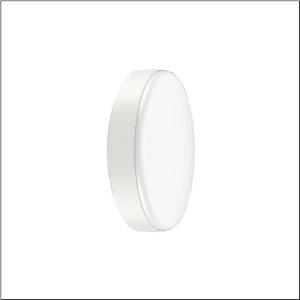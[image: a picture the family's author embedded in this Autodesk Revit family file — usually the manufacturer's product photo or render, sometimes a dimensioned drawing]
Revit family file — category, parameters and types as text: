
# Revit family: rondel_31_51wc10db34as
name_source: partatom
category: Lighting Fixtures
units: mm (PartAtom-declared; Revit-internal decimal feet)

## family parameters
Cut with Voids When Loaded = No
Host = Face
Light Source = No
Part Type = Normal
Room Calculation Point = No
Round Connector Dimension = Use Diameter
Shared = No

## types (1)
- Rondel 31 (1 x LED, 4250 lm, 35.4 W, 3000K)
    Apparent Load = 35 VA
    CIE Flux Codes = 44 75 94 94 100
    Color Rendering = 80
    Color Temperature = 3000K
    Default Elevation = 1800 mm
    Description = Rondel 31, wall and ceiling luminaire, primary optical cover: cover, of PC, opal, light emission: direct distribution, primary light characteristic: symmetric, installation type: surface-mounted, LED, rated luminous flux: 4.250lm, luminous efficacy: 120lm/W, light colour: 830, colour temperature: 3000K, with terminal, 5-pole, max. 2.5mm², mains connection: 220..240V, AC, 50/60Hz, rated input power: 35.5W, luminaire housing, of PC, traffic white (RAL 9016), diameter: 480mm, brightness and presence sensor, HF sensor, protection rating (complete): IP65, insulation class (complete): insulation class II (safety insulation), certification: CE, impact resistance: IK10, permissible operating ambient temperature: -20..+40°C, permissible storage temperature: -20..+60°C, packaging unit: 1 piece
    Height = 97 mm
    Lamp = 1 x LED
    Lamp Light Flux = 4250 lm
    Lamp Power = 35.4 W
    Lamp count = 1
    Length = 480 mm
    Luminous efficacy = 120 lm/W
    Manufacturer = Siteco
    ModVariant = No
    Model = 51WC10DB34AS
    Mounting Place = Ceiling
    Mounting Type = Surface mounted
    Number of Poles = 1
    OnlyDefault = Yes
    Power Factor = 1
    Product Name = Rondel 31
    Product group = wall and ceiling luminaire
    ProductGroupID = 302
    Protection Class = Protection class II
    Protection Degree = IP 65
    RLX_Detail_Level = 1
    RLX_Emergency_Light_Flux = 0 lm
    RLX_Emergency_Type = 0
    RLX_Emergency_Type_DB = No
    RlxData = <blob elided: 40853 chars, md5=f7e8a1e5>
    Socket = socket
    Standby Power = 0 W
    System Light Flux = 4250 lm
    System Power = 35 W
    Type Comments = Product without accessories
    Type Image = l_1007188.jpg
    URL = http://relux.com
    VarID = ---
    Voltage = 0 V
    Weight = 0.00 kg
    Width = 0 mm  [stored 0 ft]

note: [stored X ft] marks values corroborated as IEEE doubles in the binary element streams (Revit-internal decimal feet)

## geometry (parser evidence)
native form markers: Blend x4, Sweep x12
no freeform markers — native parametric forms only
